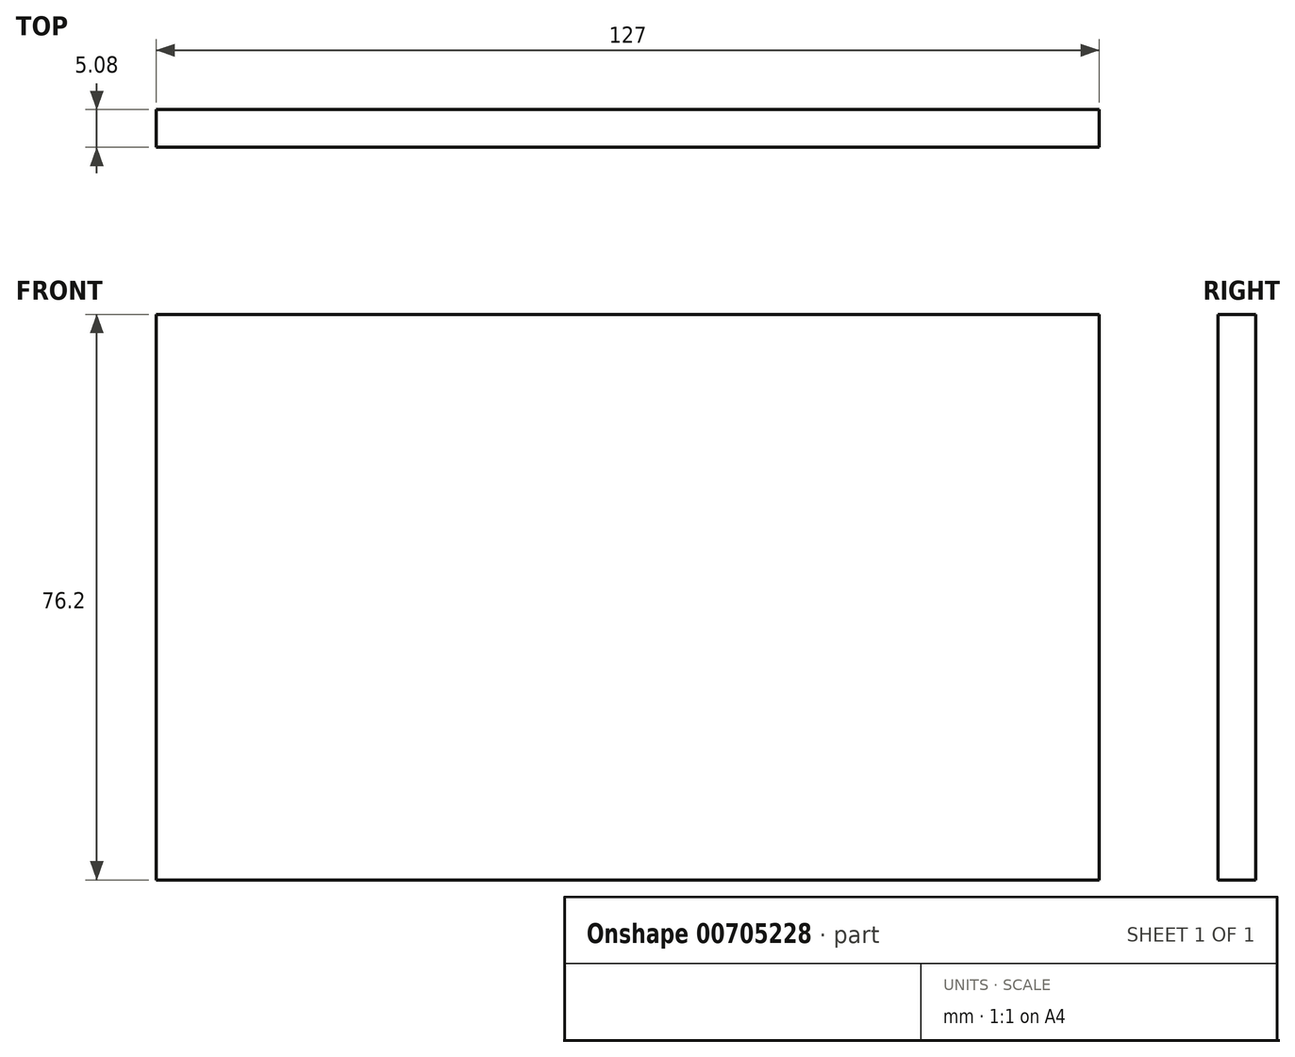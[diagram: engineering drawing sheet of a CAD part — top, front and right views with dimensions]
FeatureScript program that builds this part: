
annotation { "Feature Type Name" : "Feature", "Feature Type Description" : "" }
export const myFeature = defineFeature(function(context is Context, id is Id, definition is map)
    precondition{}
    {
        {
            var Q0;
            Q0=qCreatedBy(makeId("Front.planeOp"),FACE);
            var sketch = newSketch(context, id + "F0", { "sketchPlane" : qUnion([Q0])});
            skLineSegment(sketch, "E0.bottom", {"start": v(63.5, 37.03) * mm, "end": v(-63.5, 37.03) * mm});
            skLineSegment(sketch, "E0.top", {"start": v(63.5, -39.17) * mm, "end": v(-63.5, -39.17) * mm});
            skLineSegment(sketch, "E0.left", {"start": v(63.5, 37.03) * mm, "end": v(63.5, -39.17) * mm});
            skLineSegment(sketch, "E0.right", {"start": v(-63.5, 37.03) * mm, "end": v(-63.5, -39.17) * mm});
            skPoint(sketch, "E0.middle", {"position": v(0, -1.07) * mm});
            skSolve(sketch);
        }
        {
            var Q0;
            Q0=makeQuery(id+"F0.imprint","IMPRINT",FACE,{"disambiguationData":[TD([[makeQuery(id+"F0.imprint","IMPRINT",EDGE,{"derivedFrom":sQuery(id+"F0.wireOp",EDGE,"E0.bottom")}),1.0]])]});
            var sketch = newSketch(context, id + "F1", { "sketchPlane" : qUnion([Q0])});
            skSolve(sketch);
        }
        {
            var Q0;
            Q0 = qSketchRegion(id + "F1", true);
            var Q1;
            Q1=makeQuery(id+"F1.imprint","IMPRINT",FACE,{"disambiguationData":[TD([[makeQuery(id+"F1.imprint","IMPRINT",EDGE,{"derivedFrom":makeQuery(id+"F0.imprint","IMPRINT",EDGE,{"derivedFrom":sQuery(id+"F0.wireOp",EDGE,"E0.bottom")})}),1.0]])]});
            extrude(context, id + "F2", {"entities" : qUnion([Q0, Q1]), "depth" : 2.54 * mm, "offsetDistance" : 25.4 * mm});
        }
        {
            var Q0;
            Q0=makeQuery(id+"F2.opExtrude","CAP_FACE",FACE,{"disambiguationData":[OSD([sQuery(id+"F0.wireOp",EDGE,"E0.bottom"),sQuery(id+"F0.wireOp",EDGE,"E0.top"),sQuery(id+"F0.wireOp",EDGE,"E0.left"),sQuery(id+"F0.wireOp",EDGE,"E0.right")])],"isStart":false});
            var sketch = newSketch(context, id + "F3", { "sketchPlane" : qUnion([Q0])});
            skSolve(sketch);
        }
        {
            var Q0;
            Q0=makeQuery(id+"F0.imprint","IMPRINT",FACE,{"disambiguationData":[TD([[makeQuery(id+"F0.imprint","IMPRINT",EDGE,{"derivedFrom":sQuery(id+"F0.wireOp",EDGE,"E0.bottom")}),1.0]])]});
            var sketch = newSketch(context, id + "F4", { "sketchPlane" : qUnion([Q0])});
            skSolve(sketch);
        }
        {
            var Q0;
            Q0 = qSketchRegion(id + "F4", true);
            var Q1;
            Q1=makeQuery(id+"F3.imprint","IMPRINT",FACE,{"disambiguationData":[TD([[makeQuery(id+"F3.imprint","IMPRINT",EDGE,{"derivedFrom":makeQuery(id+"F2.opExtrude","CAP_EDGE",EDGE,{"disambiguationData":[OSD([sQuery(id+"F0.wireOp",EDGE,"E0.bottom")])],"isStart":false})}),1.0]])]});
            extrude(context, id + "F5", {"entities" : qUnion([Q0, Q1]), "operationType" : NewBodyOperationType.ADD, "depth" : 2.54 * mm, "offsetDistance" : 25.4 * mm});
        }
    });
